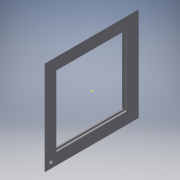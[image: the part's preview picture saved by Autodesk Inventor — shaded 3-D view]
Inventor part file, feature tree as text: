
AUTODESK INVENTOR PART (.ipt)
format: ipt  version: 2018.3 (Build 223284000, 284)  size: 164,864 bytes
history: native  units: mm
features: reference x21, sketch x6, extrude x4, projected_geometry x3, other x3, chamfer x2, hole x1
ambient origin geometry x8: Origin, YZ Plane, XZ Plane, XY Plane, X Axis, Y Axis, Z Axis, Center Point
bodies: Volumenkörper1 (feature_tree)
feature tree (40):
  extrude  "Extrusion1"  Depth=540.0mm
  extrude  "Extrusion2"  Depth=67.0mm
  extrude  "Extrusion3"  Depth=67.0mm
  sketch  "Skizze6"  dims[d7=67.0mm d8=10.0mm d9=0.0mm]
  chamfer  "Fase1"  Distance=10.0mm
  chamfer  "Fase2"  Distance=10.0mm
  extrude  "Extrusion7"  Depth=10.0mm
  sketch  "Skizze8"  dims[d10=10.0mm]
  hole  "Bohrung2"  [1 undecoded]
  sketch  "Skizze1"  dims[d0=540.0mm d1=540.0mm]
  sketch  "Skizze2"  dims[d2=18.0mm d3=0.0mm d4=67.0mm]
  projected_geometry  "Projizierte Kontur1"
  sketch  "Skizze3"  dims[d5=67.0mm d6=67.0mm]
  projected_geometry  "Projizierte Kontur2"
  projected_geometry  "Projizierte Kontur4"
  reference  "Referenz29"
  reference  "Referenz30"
  reference  "Referenz31"
  reference  "Referenz32"
  reference  "Referenz33"
  reference  "Referenz34"
  reference  "Referenz35"
  reference  "Referenz36"
  reference  "Referenz37"
  reference  "Referenz38"
  reference  "Referenz39"
  reference  "Referenz40"
  reference  "Referenz41"
  reference  "Referenz42"
  reference  "Referenz43"
  reference  "Referenz44"
  reference  "Referenz45"
  reference  "Referenz46"
  reference  "Referenz47"
  reference  "Referenz48"
  reference  "Referenz49"
  sketch  "Skizze9"  dims[d11=10.0mm d12=10.0mm d13=10.0mm d14=8.0mm d15=0.0mm d26=18.0mm d27=2.0mm d28=45.0deg d31=18.0mm d32=2.0mm d33=45.0deg d34=50.0mm d37=50.0mm d38=15.0mm d39=0.0mm d40=38.0mm d41=33.0mm d42=20.0mm d43=6.0mm d44=4.0mm d45=2.0mm d46=90.0deg d47=18.0mm d48=20.594885mm]
  parser-record x1  (decoder bookkeeping rows leaked as tree rows — omitted from the tree; the rows remain in map.json)
  other  "Baugruppe1.iam"
  other  "PV_Modul_CPY_3:1"
note: 1 required parameter value undecoded (feature->parameter linkage not recoverable at this tier; creation-order binding heuristic only, values carry confidence <= 0.55)
note: 1 file-system path scrubbed to <path> (originals preserved in map.json)
